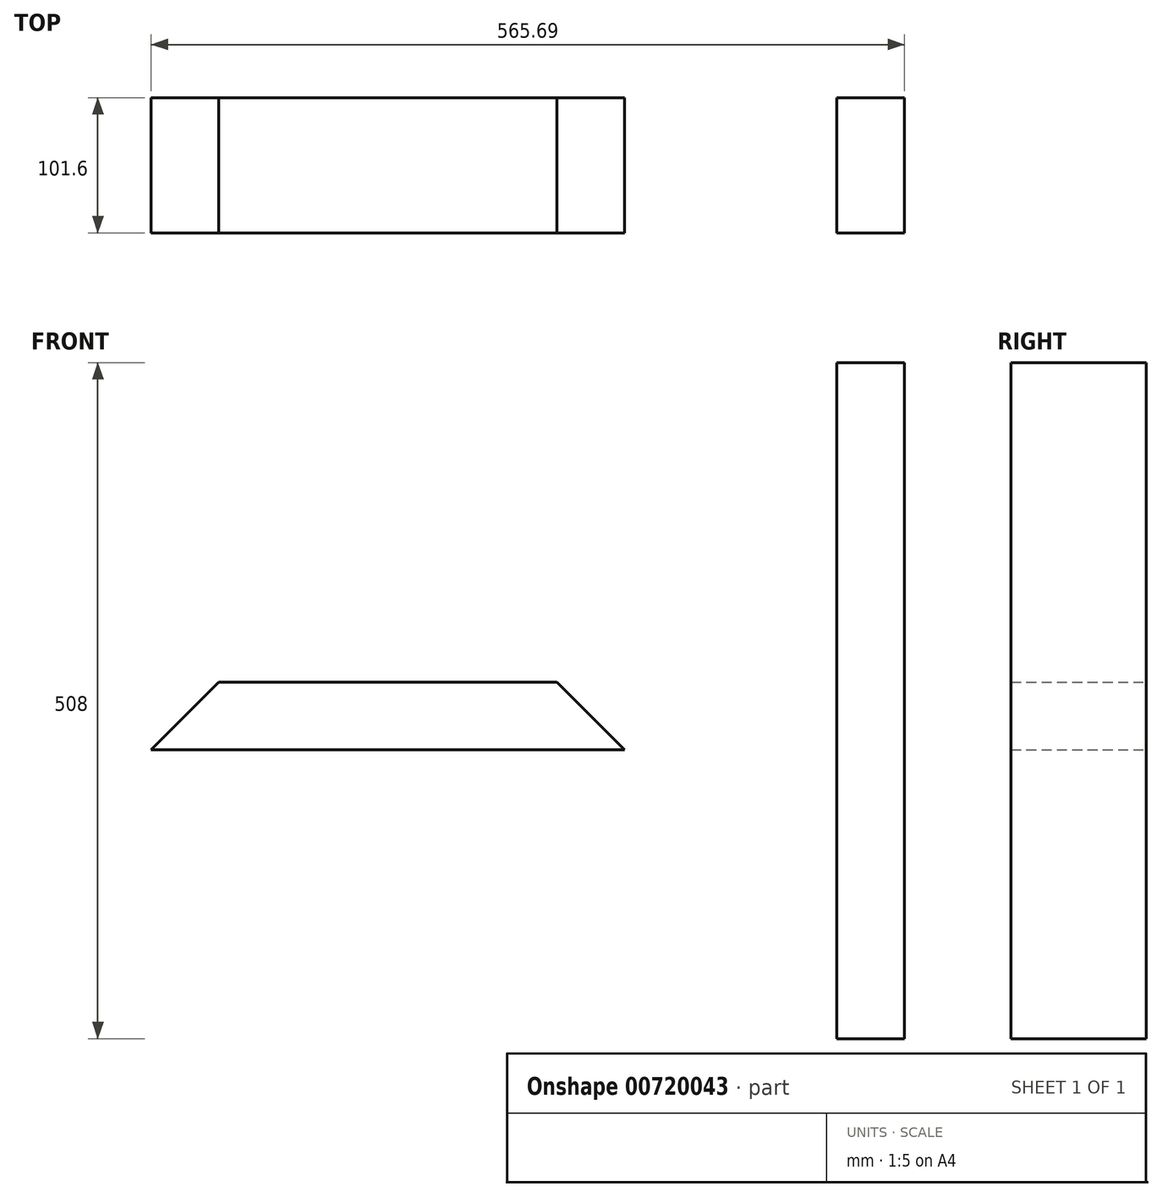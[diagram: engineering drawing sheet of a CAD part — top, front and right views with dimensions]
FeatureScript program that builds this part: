
annotation { "Feature Type Name" : "Feature", "Feature Type Description" : "" }
export const myFeature = defineFeature(function(context is Context, id is Id, definition is map)
    precondition{}
    {
        {
            var Q0;
            Q0=qCreatedBy(makeId("Front.planeOp"),FACE);
            var sketch = newSketch(context, id + "F0", { "sketchPlane" : qUnion([Q0])});
            skLineSegment(sketch, "E0.bottom", {"start": v(-25.4, 254) * mm, "end": v(25.4, 254) * mm});
            skLineSegment(sketch, "E0.top", {"start": v(-25.4, -254) * mm, "end": v(25.4, -254) * mm});
            skLineSegment(sketch, "E0.left", {"start": v(-25.4, 254) * mm, "end": v(-25.4, -254) * mm});
            skLineSegment(sketch, "E0.right", {"start": v(25.4, 254) * mm, "end": v(25.4, -254) * mm});
            skPoint(sketch, "E0.middle", {"position": v(0, 0) * mm});
            skSolve(sketch);
        }
        {
            var Q0;
            Q0=qCreatedBy(makeId("Front.planeOp"),FACE);
            var sketch = newSketch(context, id + "F1", { "sketchPlane" : qUnion([Q0])});
            skLineSegment(sketch, "E1", {"start": v(-540.3, -36.98) * mm, "end": v(-184.7, -36.98) * mm});
            skLineSegment(sketch, "E2", {"start": v(-184.7, -36.98) * mm, "end": v(-235.5, 13.82) * mm});
            skLineSegment(sketch, "E3", {"start": v(-235.5, 13.82) * mm, "end": v(-489.5, 13.82) * mm});
            skLineSegment(sketch, "E4", {"start": v(-489.5, 13.82) * mm, "end": v(-540.3, -36.98) * mm});
            skSolve(sketch);
        }
        {
            var Q0;
            Q0=makeQuery(id+"F1.imprint","IMPRINT",FACE,{"disambiguationData":[TD([[makeQuery(id+"F1.imprint","IMPRINT",EDGE,{"derivedFrom":sQuery(id+"F1.wireOp",EDGE,"E1")}),1.0]])]});
            extrude(context, id + "F2", {"entities" : qUnion([Q0]), "endBound" : BoundingType.SYMMETRIC, "depth" : 101.6 * mm, "offsetDistance" : 25.4 * mm});
        }
        {
            var Q0;
            Q0=makeQuery(id+"F0.imprint","IMPRINT",FACE,{"disambiguationData":[TD([[makeQuery(id+"F0.imprint","IMPRINT",EDGE,{"derivedFrom":sQuery(id+"F0.wireOp",EDGE,"E0.bottom")}),-1.0]])]});
            extrude(context, id + "F3", {"entities" : qUnion([Q0]), "endBound" : BoundingType.SYMMETRIC, "depth" : 101.6 * mm, "offsetDistance" : 25.4 * mm});
        }
    });
